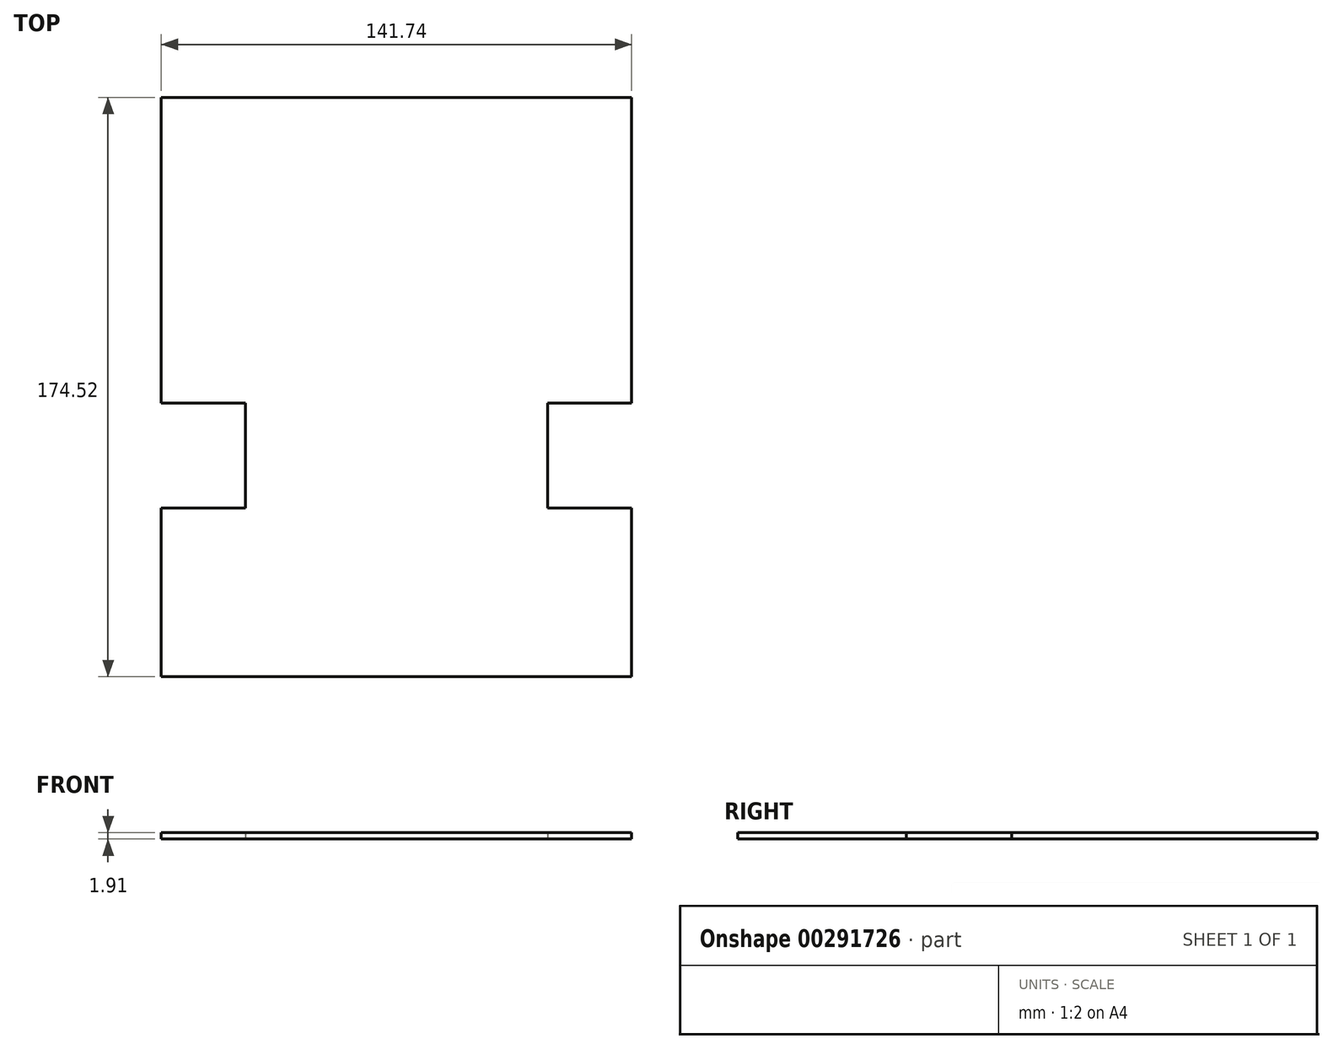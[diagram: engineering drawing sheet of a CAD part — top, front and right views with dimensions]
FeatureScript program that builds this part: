
annotation { "Feature Type Name" : "Feature", "Feature Type Description" : "" }
export const myFeature = defineFeature(function(context is Context, id is Id, definition is map)
    precondition{}
    {
        {
            var Q0;
            Q0=qCreatedBy(makeId("Top.planeOp"),FACE);
            var sketch = newSketch(context, id + "F0", { "sketchPlane" : qUnion([Q0])});
            skLineSegment(sketch, "E0", {"start": v(0, 70.73) * mm, "end": v(70.87, 70.73) * mm});
            skLineSegment(sketch, "E1", {"start": v(70.87, 70.73) * mm, "end": v(70.87, -21.29) * mm});
            skLineSegment(sketch, "E2", {"start": v(70.87, -21.29) * mm, "end": v(45.5, -21.29) * mm});
            skLineSegment(sketch, "E3", {"start": v(45.5, -21.29) * mm, "end": v(45.5, -53.02) * mm});
            skLineSegment(sketch, "E4", {"start": v(45.5, -53.02) * mm, "end": v(70.87, -53.02) * mm});
            skLineSegment(sketch, "E5", {"start": v(70.87, -53.02) * mm, "end": v(70.87, -103.79) * mm});
            skLineSegment(sketch, "E6", {"start": v(70.87, -103.79) * mm, "end": v(0, -103.79) * mm});
            skLineSegment(sketch, "E7.MirrorCS", {"start": v(0, 70.73) * mm, "end": v(-70.87, 70.73) * mm});
            skLineSegment(sketch, "E8.MirrorCS", {"start": v(-70.87, 70.73) * mm, "end": v(-70.87, -21.29) * mm});
            skLineSegment(sketch, "E9.MirrorCS", {"start": v(-70.87, -21.29) * mm, "end": v(-45.5, -21.29) * mm});
            skLineSegment(sketch, "E10.MirrorCS", {"start": v(-45.5, -21.29) * mm, "end": v(-45.5, -53.02) * mm});
            skLineSegment(sketch, "E11.MirrorCS", {"start": v(-45.5, -53.02) * mm, "end": v(-70.87, -53.02) * mm});
            skLineSegment(sketch, "E12.MirrorCS", {"start": v(-70.87, -53.02) * mm, "end": v(-70.87, -103.79) * mm});
            skLineSegment(sketch, "E13.MirrorCS", {"start": v(-70.87, -103.79) * mm, "end": v(0, -103.79) * mm});
            skSolve(sketch);
        }
        {
            var Q0;
            Q0=makeQuery(id+"F0.imprint","IMPRINT",FACE,{"disambiguationData":[TD([[makeQuery(id+"F0.imprint","IMPRINT",EDGE,{"derivedFrom":sQuery(id+"F0.wireOp",EDGE,"E0")}),-1.0]])]});
            extrude(context, id + "F1", {"entities" : qUnion([Q0]), "depth" : 1.9 * mm});
        }
    });
